# Revit family: VT.0600.0.06
name_source: partatom
category: Оборудование
units: mm (PartAtom-declared; Revit-internal decimal feet)

## family parameters
Всегда вертикально = Да
Заголовок OmniClass = Climate Control (HVAC)
На основе рабочей плоскости = Нет
Номер OmniClass = 23.75.00.00
Общий = Нет
При загрузке вырезать с полостями = Нет
Размер круглого соединителя = Использовать диаметр
Тип детали = Нормальный
Точка расчета площади = Нет

## types (2) — shared parameters
Article Description = Male cap
Article Type = AC 600
Brand url = http://www.ivar-group.com
Discharge of responsability = BIM models made by I.V.A.R. S.p.A. are designed as an aid to design and they must be always verified by the end user. I.V.A.R. S.p.A. has no responsibility for any direct or indirect damages of any kind, deriving or resulting from the use of such files.
EMCS Version = 3.0
Family Version = Rev.00
Installation instructions = https://www.ivar-group.com
LOD = LOD400
Manifacturer URL = https://www.ivar-group.com
Produced in = Made in Italy
Product Guid = 9f5aa4b1-e878-4bce-a46d-16af8262626e
Product Line = THERMAL POWER STATION
Product certification = https://www.ivar-group.com
Product data url = https://bimobject.com
Product url = https://www.ivar-group.com
Revit Version = 2018
SKU продукта = VARIMIX
Technical description = https://www.ivar-group.com
URL = https://www.ivar-group.com
Uniformat II Описание = HVAC
Вес нетто (кг) = 0
Группа модели = AC 600
Группа продуктов = Varimix
Изготовитель = IVAR
Материал основной = Brass
Название производителя = IVAR
Описание = Male cap
Страна производитель = Italy
zero-valued in all types: Номинальная высота, Номинальная ширина

## per-type parameters (varying)
| type | BIMобъект категории | BIMобъект основная категория | Finishing | Uniclass 1.4 Описание | Uniclass 2.0 Описание | Uniclass 2015 Name | Классификация IFC | Код категории BIMобъекта | Код основной категории BIMobject | Мастерформат 2014 Описание | Материал | Описание NBS | Описание OmniClass | Описание Конфигурации | Практическое руководство по использованию семьи | Размер соединения | Семейство продуктов |
| Nickel | Другое | Водопровод | Brass - Nickel | Климат-контроль установки и оборудование (HVAC) | Арматура | Системы отопления, охлаждения и охлаждения | Клапан | водопроводным-другой | водопровод | Отопление, вентиляция и кондиционирование воздуха (HVAC) | Nickel plated brass - CW617N | Арматура | HVAC Специальные продукты и оборудование | Пробка | - Вы должны выбрать один и только один тип отделочного материала для мужской кепки. Отметьте эту опцию в «Название типа - Никель» или «Название типа - Желтый». | G 1"1/4 M | Тепловая электростанция |
| Yellow | Other | Plumbing | BRASS - CW617N | Climate control plant and equipment (HVAC) | Valves | Heating, cooling and refrigeration systems | Valve | plumbing-other | plumbing | Heating, Ventilating, and Air Conditioning (HVAC) | Brass - CW617N | Valves | HVAC Specific Products and Equipment | Male cap. | You have to choose one and only one type of finishing material for male cap. Check this option in “Name of type – Nickel” or “Name of type – Yellow”. | 1"1/4 | Thermal Power Station |
